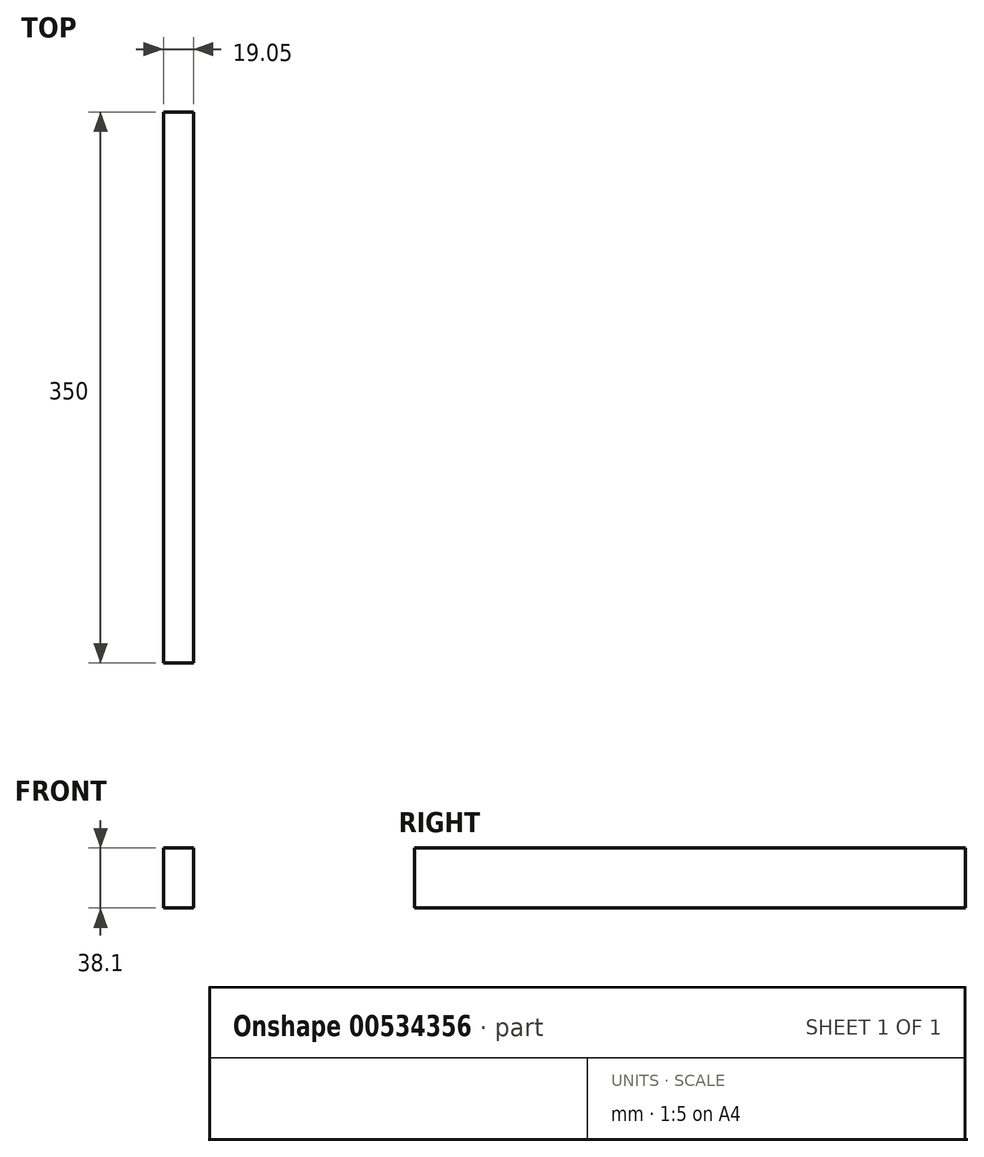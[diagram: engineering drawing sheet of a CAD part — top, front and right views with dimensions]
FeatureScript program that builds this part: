
annotation { "Feature Type Name" : "Feature", "Feature Type Description" : "" }
export const myFeature = defineFeature(function(context is Context, id is Id, definition is map)
    precondition{}
    {
        {
            var Q0;
            Q0=qCreatedBy(makeId("Front.planeOp"),FACE);
            var sketch = newSketch(context, id + "F0", { "sketchPlane" : qUnion([Q0])});
            skLineSegment(sketch, "E0.bottom", {"start": v(0, 0) * mm, "end": v(19.05, 0) * mm});
            skLineSegment(sketch, "E0.top", {"start": v(0, 38.1) * mm, "end": v(19.05, 38.1) * mm});
            skLineSegment(sketch, "E0.left", {"start": v(0, 0) * mm, "end": v(0, 38.1) * mm});
            skLineSegment(sketch, "E0.right", {"start": v(19.05, 0) * mm, "end": v(19.05, 38.1) * mm});
            skSolve(sketch);
        }
        {
            var Q0;
            Q0=makeQuery(id+"F0.imprint","IMPRINT",FACE,{"disambiguationData":[TD([[makeQuery(id+"F0.imprint","IMPRINT",EDGE,{"derivedFrom":sQuery(id+"F0.wireOp",EDGE,"E0.bottom")}),1.0]])]});
            extrude(context, id + "F1", {"entities" : qUnion([Q0]), "depth" : 350 * mm, "offsetDistance" : 25 * mm});
        }
    });
